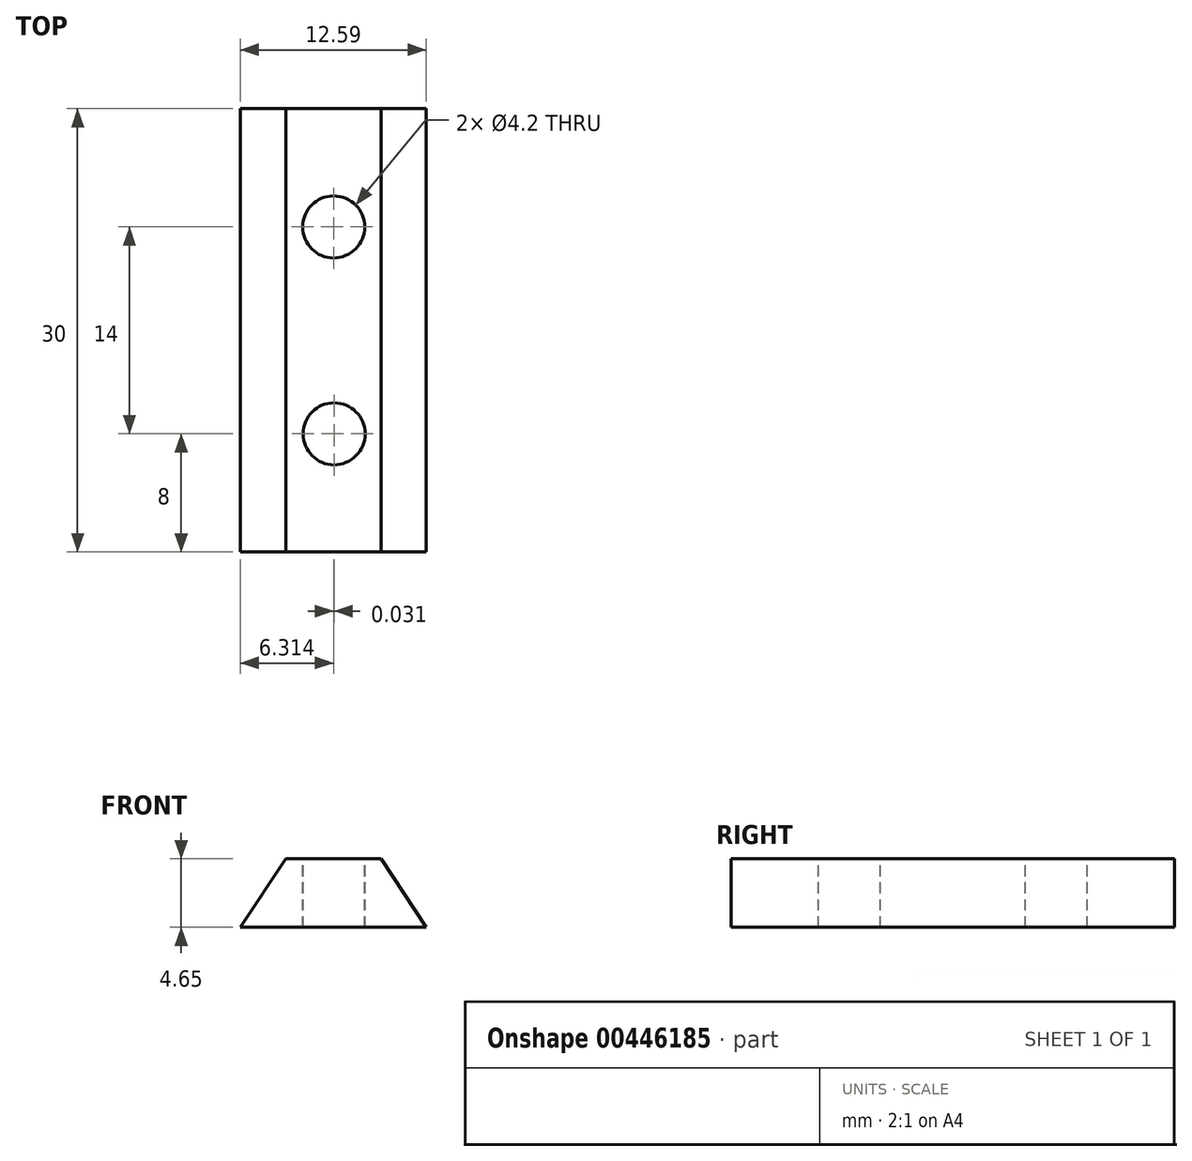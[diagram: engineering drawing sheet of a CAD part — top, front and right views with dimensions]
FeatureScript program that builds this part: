
annotation { "Feature Type Name" : "Feature", "Feature Type Description" : "" }
export const myFeature = defineFeature(function(context is Context, id is Id, definition is map)
    precondition{}
    {
        {
            var Q0;
            Q0=qCreatedBy(makeId("Front.planeOp"),FACE);
            var sketch = newSketch(context, id + "F0", { "sketchPlane" : qUnion([Q0])});
            skLineSegment(sketch, "E0", {"start": v(-12.59, 0) * mm, "end": v(0.06, 0) * mm});
            skLineSegment(sketch, "E1", {"start": v(0, 0) * mm, "end": v(-3.07, 4.65) * mm});
            skLineSegment(sketch, "E2", {"start": v(-3.07, 4.65) * mm, "end": v(-9.52, 4.65) * mm});
            skLineSegment(sketch, "E3", {"start": v(-9.52, 4.65) * mm, "end": v(-12.59, 0) * mm});
            skSolve(sketch);
        }
        {
            var Q0;
            {var subQ2=sQuery(id+"F0.wireOp",EDGE,"E1");Q0=makeQuery(id+"F0.imprint","IMPRINT",FACE,{"disambiguationData":[TD([[makeQuery(id+"F0.imprint","IMPRINT",EDGE,{"derivedFrom":subQ2}),1.0]])]});}
            extrude(context, id + "F1", {"entities" : qUnion([Q0]), "depth" : 30 * mm});
        }
        {
            var Q0;
            Q0=makeQuery(id+"F1.opExtrude","SWEPT_FACE",FACE,{"disambiguationData":[OSD([sQuery(id+"F0.wireOp",EDGE,"E2")])]});
            var sketch = newSketch(context, id + "F2", { "sketchPlane" : qUnion([Q0])});
            skCircle(sketch, "E4", {"center": v(-6.28, -8) * mm, "radius": 2.1 * mm});
            skCircle(sketch, "E5", {"center": v(-6.25, -22) * mm, "radius": 2.1 * mm});
            skLineSegment(sketch, "E6", {"start": v(-6.3, 0) * mm, "end": v(-6.3, -30) * mm});
            skSolve(sketch);
        }
        {
            var Q0;
            {var subQ0=sQuery(id+"F2.wireOp",EDGE,"E6");var subQ1=sQuery(id+"F2.wireOp",EDGE,"E4");var subQ2=makeQuery(id+"F2.imprint","INTERSECT",VERTEX,{"disambiguationData":[OD(0.0)],"derivedFrom":[subQ1,subQ0]});Q0=makeQuery(id+"F2.imprint","IMPRINT",FACE,{"disambiguationData":[TD([[makeQuery(id+"F2.imprint","IMPRINT",EDGE,{"disambiguationData":[TD([[subQ2,-1.0]])],"derivedFrom":subQ1}),1.0]])]});}
            var Q1;
            {var subQ0=sQuery(id+"F2.wireOp",EDGE,"E6");var subQ1=sQuery(id+"F2.wireOp",EDGE,"E4");var subQ2=makeQuery(id+"F2.imprint","INTERSECT",VERTEX,{"disambiguationData":[OD(0.0)],"derivedFrom":[subQ1,subQ0]});Q1=makeQuery(id+"F2.imprint","IMPRINT",FACE,{"disambiguationData":[TD([[makeQuery(id+"F2.imprint","IMPRINT",EDGE,{"disambiguationData":[TD([[subQ2,1.0]])],"derivedFrom":subQ1}),1.0]])]});}
            var Q2;
            {var subQ0=sQuery(id+"F2.wireOp",EDGE,"E6");var subQ1=sQuery(id+"F2.wireOp",EDGE,"E5");var subQ2=makeQuery(id+"F2.imprint","INTERSECT",VERTEX,{"disambiguationData":[OD(0.0)],"derivedFrom":[subQ1,subQ0]});Q2=makeQuery(id+"F2.imprint","IMPRINT",FACE,{"disambiguationData":[TD([[makeQuery(id+"F2.imprint","IMPRINT",EDGE,{"disambiguationData":[TD([[subQ2,-1.0]])],"derivedFrom":subQ1}),1.0]])]});}
            var Q3;
            {var subQ0=sQuery(id+"F2.wireOp",EDGE,"E6");var subQ1=sQuery(id+"F2.wireOp",EDGE,"E5");var subQ2=makeQuery(id+"F2.imprint","INTERSECT",VERTEX,{"disambiguationData":[OD(0.0)],"derivedFrom":[subQ1,subQ0]});Q3=makeQuery(id+"F2.imprint","IMPRINT",FACE,{"disambiguationData":[TD([[makeQuery(id+"F2.imprint","IMPRINT",EDGE,{"disambiguationData":[TD([[subQ2,1.0]])],"derivedFrom":subQ1}),1.0]])]});}
            extrude(context, id + "F3", {"entities" : qUnion([Q0, Q1, Q2, Q3]), "operationType" : NewBodyOperationType.REMOVE, "endBound" : BoundingType.THROUGH_ALL, "oppositeDirection" : true, "depth" : 25 * mm});
        }
    });
